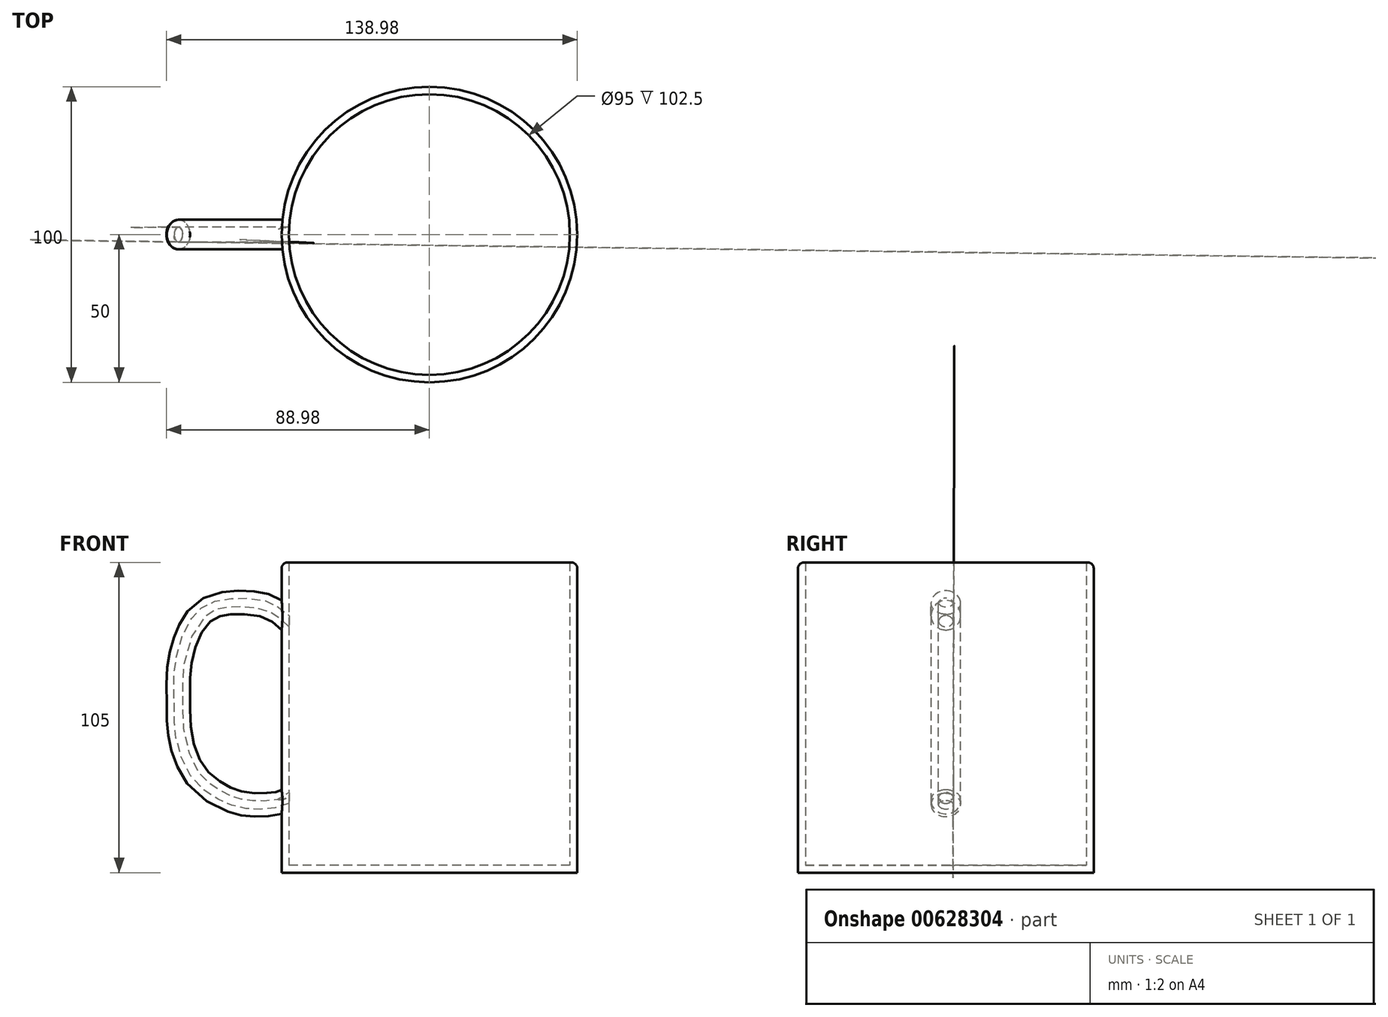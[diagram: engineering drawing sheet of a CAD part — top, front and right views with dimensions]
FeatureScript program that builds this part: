
annotation { "Feature Type Name" : "Feature", "Feature Type Description" : "" }
export const myFeature = defineFeature(function(context is Context, id is Id, definition is map)
    precondition{}
    {
        {
            var Q0;
            Q0=qCreatedBy(makeId("Top.planeOp"),FACE);
            var sketch = newSketch(context, id + "F0", { "sketchPlane" : qUnion([Q0])});
            skCircle(sketch, "E0", {"center": v(0, 0) * mm, "radius": 50 * mm});
            skSolve(sketch);
        }
        {
            var Q0;
            Q0=makeQuery(id+"F0.imprint","IMPRINT",FACE,{"disambiguationData":[TD([[makeQuery(id+"F0.imprint","IMPRINT",EDGE,{"derivedFrom":sQuery(id+"F0.wireOp",EDGE,"E0")}),1.0]])]});
            extrude(context, id + "F1", {"entities" : qUnion([Q0]), "depth" : 105 * mm, "offsetDistance" : 25.4 * mm});
        }
        {
            var Q0;
            Q0=qCreatedBy(makeId("Front.planeOp"),FACE);
            var sketch = newSketch(context, id + "F2", { "sketchPlane" : qUnion([Q0])});
            skFitSpline(sketch, "E1", {"points": [v(-48.1, 84.86) * mm, v(-55.28, 89.46) * mm, v(-66.77, 90.6) * mm, v(-74.81, 88.3) * mm, v(-80.56, 81.42) * mm, v(-84, 69.36) * mm, v(-84.29, 59.3) * mm, v(-83.71, 46.95) * mm, v(-78.26, 33.17) * mm, v(-69.36, 26.28) * mm, v(-62.18, 23.98) * mm, v(-53.56, 23.98) * mm, v(-47.82, 26) * mm, v(-45.52, 28.29) * mm], "startDerivative": vector(-87.02, 72.24) * mm, "endDerivative": vector(42.56, 53.17) * mm});
            skSolve(sketch);
        }
        {
            var Q0;
            Q0=qCreatedBy(makeId("Right.planeOp"),FACE);
            cPlane(context, id + "F3", {"entities" : qUnion([Q0]), "cplaneType" : CPlaneType.OFFSET, "offset" : 50 * mm, "oppositeDirection" : true, "width" : 152.4 * mm, "height" : 152.4 * mm});
        }
        {
            var Q0;
            Q0=qCreatedBy(id+"F3.planeOp",FACE);
            var sketch = newSketch(context, id + "F4", { "sketchPlane" : qUnion([Q0])});
            skCircle(sketch, "E2", {"center": v(0, 87.16) * mm, "radius": 5 * mm});
            skSolve(sketch);
        }
        {
            var Q0;
            Q0=makeQuery(id+"F4.imprint","IMPRINT",FACE,{"disambiguationData":[TD([[makeQuery(id+"F4.imprint","IMPRINT",EDGE,{"derivedFrom":sQuery(id+"F4.wireOp",EDGE,"E2")}),1.0]])]});
            var Q1;
            Q1=sQuery(id+"F4.wireOp",EDGE,"E2");
            var Q2;
            Q2=sQuery(id+"F2.wireOp",EDGE,"E1");
            sweep(context, id + "F5", {"operationType" : NewBodyOperationType.ADD, "profiles" : qUnion([Q0]), "surfaceProfiles" : qUnion([Q1]), "path" : qUnion([Q2])});
        }
        {
            var Q0;
            Q0=makeQuery(id+"F1.opExtrude","CAP_FACE",FACE,{"disambiguationData":[OSD([sQuery(id+"F0.wireOp",EDGE,"E0")])],"isStart":false});
            shell(context, id + "F6", {"entities" : qUnion([Q0]), "thickness" : 2.5 * mm});
        }
        {
            var Q0;
            Q0=makeQuery(id+"F1.opExtrude","CAP_EDGE",EDGE,{"disambiguationData":[OSD([sQuery(id+"F0.wireOp",EDGE,"E0")])],"isStart":false});
            fillet(context, id + "F7", {"entities" : qUnion([Q0]), "radius" : 2 * mm, "tangentPropagation" : true, "allowEdgeOverflow" : false});
        }
    });
